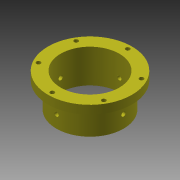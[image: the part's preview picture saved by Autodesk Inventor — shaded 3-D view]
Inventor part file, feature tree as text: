
AUTODESK INVENTOR PART (.ipt)
format: ipt  version: 2015 (Build 190159000, 159)  size: 583,680 bytes
history: native  units: in
note: dims shown in document units (in); Inventor stores cm internally (conversion verified against a paired STEP export)
features: thread x28, other x14, fillet x11, sketch x11, plane x7, projected_geometry x6, extrude x5, hole x5, mirror x3, pattern_circular x2, boolean_combine x1
ambient origin geometry x8: Origin, YZ Plane, XZ Plane, XY Plane, X Axis, Y Axis, Z Axis, Center Point
bodies: Solid6 (feature_tree)
feature tree (93):
  other  "board_with_hole_pipes.ipt"
  other  "Layout with const "
  plane  "Work Plane1"
  extrude  "Extrusion1"  Depth=18.0in
  extrude  "Extrusion2"  Depth=23.5in
  hole  "Hole1"  [1 undecoded]
  pattern_circular  "Circular Pattern1"  [2 undecoded]
  plane  "Work Plane3"
  hole  "Hole2"  [1 undecoded]
  thread  "Thread2"  [1 undecoded]
  thread  "Thread3"  [1 undecoded]
  thread  "Thread4"  [1 undecoded]
  thread  "Thread5"  [1 undecoded]
  thread  "Thread6"  [1 undecoded]
  thread  "Thread7"  [1 undecoded]
  mirror  "Mirror1"
  mirror  "Mirror2"
  mirror  "Mirror3"
  plane  "Work Plane4"
  extrude  "Extrusion3"  Depth=0.25in
  thread  "Thread8"  [1 undecoded]
  thread  "Thread9"  [1 undecoded]
  thread  "Thread10"  [1 undecoded]
  thread  "Thread11"  [1 undecoded]
  thread  "Thread12"  [1 undecoded]
  thread  "Thread13"  [1 undecoded]
  thread  "Thread14"  [1 undecoded]
  thread  "Thread15"  [1 undecoded]
  thread  "Thread16"  [1 undecoded]
  thread  "Thread17"  [1 undecoded]
  thread  "Thread18"  [1 undecoded]
  thread  "Thread19"  [1 undecoded]
  thread  "Thread20"  [1 undecoded]
  thread  "Thread21"  [1 undecoded]
  thread  "Thread22"  [1 undecoded]
  thread  "Thread23"  [1 undecoded]
  thread  "Thread24"  [1 undecoded]
  thread  "Thread25"  [1 undecoded]
  extrude  "Extrusion4"  Depth=0.25in TaperAngle=0.0deg
  plane  "Work Plane7"
  extrude  "Extrusion5"  Depth=0.25in TaperAngle=0.0deg
  boolean_combine  "Combine1"
  plane  "Work Plane8"
  plane  "Work Plane9"
  hole  "Hole3"  [1 undecoded]
  hole  "Hole4"  [1 undecoded]
  thread  "Thread26"  [1 undecoded]
  thread  "Thread27"  [1 undecoded]
  thread  "Thread28"  [1 undecoded]
  thread  "Thread29"  [1 undecoded]
  fillet  "Fillet2"  Radius=1.0in
  fillet  "Fillet3"  Radius=1.0in
  fillet  "Fillet4"  Radius=1.0in
  fillet  "Fillet5"  Radius=1.0in
  fillet  "Fillet6"  Radius=1.0in
  fillet  "Fillet7"  Radius=1.0in
  fillet  "Fillet8"  Radius=1.0in
  fillet  "Fillet9"  Radius=1.0in
  fillet  "Fillet10"  Radius=1.0in
  fillet  "Fillet11"  Radius=1.0in
  fillet  "Fillet12"  Radius=2.0in
  plane  "Work Plane10"
  hole  "Hole5"  [1 undecoded]
  other  "Work Axis2"
  pattern_circular  "Circular Pattern2"  [2 undecoded]
  other  "Solid1::board_with_hole_pipes.ipt"
  other  "TaggingFeature1"
  sketch  "Sketch3"  dims[d0=0.1969in d1=18.0in]
  sketch  "Sketch4"  dims[d2=24.0in d3=23.5in]
  other  "legFL"
  sketch  "Sketch5"  dims[d4=17.5in d5=5.5in]
  sketch  "Sketch6"  dims[d6=1.5in]
  sketch  "Sketch7"  dims[d9=5.5in]
  other  "Pattern of legFL:1"
  other  "legFR"
  other  "Pattern of legFL:2"
  other  "legBR"
  other  "Pattern of legFR:3"
  other  "legBL"
  sketch  "Sketch8"  dims[d10=1.5in]
  projected_geometry  "Projected Loop2"
  sketch  "Sketch10"  dims[d11=5.5in]
  sketch  "Sketch11"  dims[d12=1.5in]
  other  "miniplat"
  sketch  "Sketch12"  dims[d15=4.0in]
  projected_geometry  "Projected Loop3"
  projected_geometry  "Projected Loop4"
  projected_geometry  "Projected Loop5"
  projected_geometry  "Projected Loop6"
  projected_geometry  "Projected Loop7"
  sketch  "Sketch13"  dims[d18=5.5in]
  sketch  "Sketch14"  dims[d19=1.5in d22=5.0in d23=3.0in d24=5.0in d25=3.0in d26=3.0in d27=3.0in d28=3.0in d29=5.0in d30=4.0in d31=3.5in d32=0.5in d33=1.0in d34=0.0in d35=0.0in d36=5.0in d37=0.5in d38=0.0in d39=0.25in d40=0.75in d41=0.375in d42=0.25in d43=0.5635in d44=1.8125in d45=0.8108in d48=2.3622in d49=360.0deg d52=0.25in d53=0.75in d54=0.375in d55=0.25in d56=0.5635in d57=1.8125in d58=0.8108in d59=1.0in d60=0.0in d61=1.0in d62=0.0in d63=1.0in d64=0.0in d65=1.0in d66=0.0in d67=1.0in d68=0.0in d69=1.0in d70=0.0in d71=3.475in d72=0.0in d73=1.0in d74=0.0in d75=1.0in d76=0.0in d77=1.0in d78=0.0in d79=1.0in d80=0.0in d81=1.0in d82=0.0in d83=1.0in d84=0.0in d85=1.0in d86=0.0in d87=1.0in d88=0.0in d89=1.0in d90=0.0in d91=1.0in d92=0.0in d93=1.0in d94=0.0in d95=1.0in d96=0.0in d97=1.0in d98=0.0in d99=1.0in d100=0.0in d101=1.0in d102=0.0in d103=1.0in d104=0.0in d105=1.0in d106=0.0in d107=1.0in d108=0.0in d109=1.0in d110=1.0in d111=1.0in d112=1.0in d113=1.0in d114=1.0in d115=2.0in d116=0.0in d117=1.0in d118=0.0in d119=0.5in d120=0.5in d121=0.5in d122=0.5in d123=0.25in d124=0.75in d125=0.375in d126=0.25in d127=0.5635in d128=2.0in d129=0.0in d130=0.5in d131=0.75in d132=0.375in d133=0.25in d134=0.5635in d135=2.0in d136=0.8108in d137=1.0in d138=0.0in d139=1.0in d140=0.0in d141=1.0in d142=0.0in d143=1.0in d144=0.0in d153=0.125in d154=0.125in d155=0.125in d166=0.125in d167=0.125in d168=0.125in d169=0.125in d170=0.125in d171=0.125in d172=0.125in d173=0.125in d174=0.25in d175=0.25in d176=0.75in d177=0.375in d178=0.25in d179=0.5635in d180=1.875in d181=0.0in d182=1.5748in d183=360.0deg]
  other  "platform"
note: 37 required parameter values undecoded (feature->parameter linkage not recoverable at this tier; creation-order binding heuristic only, values carry confidence <= 0.55)
